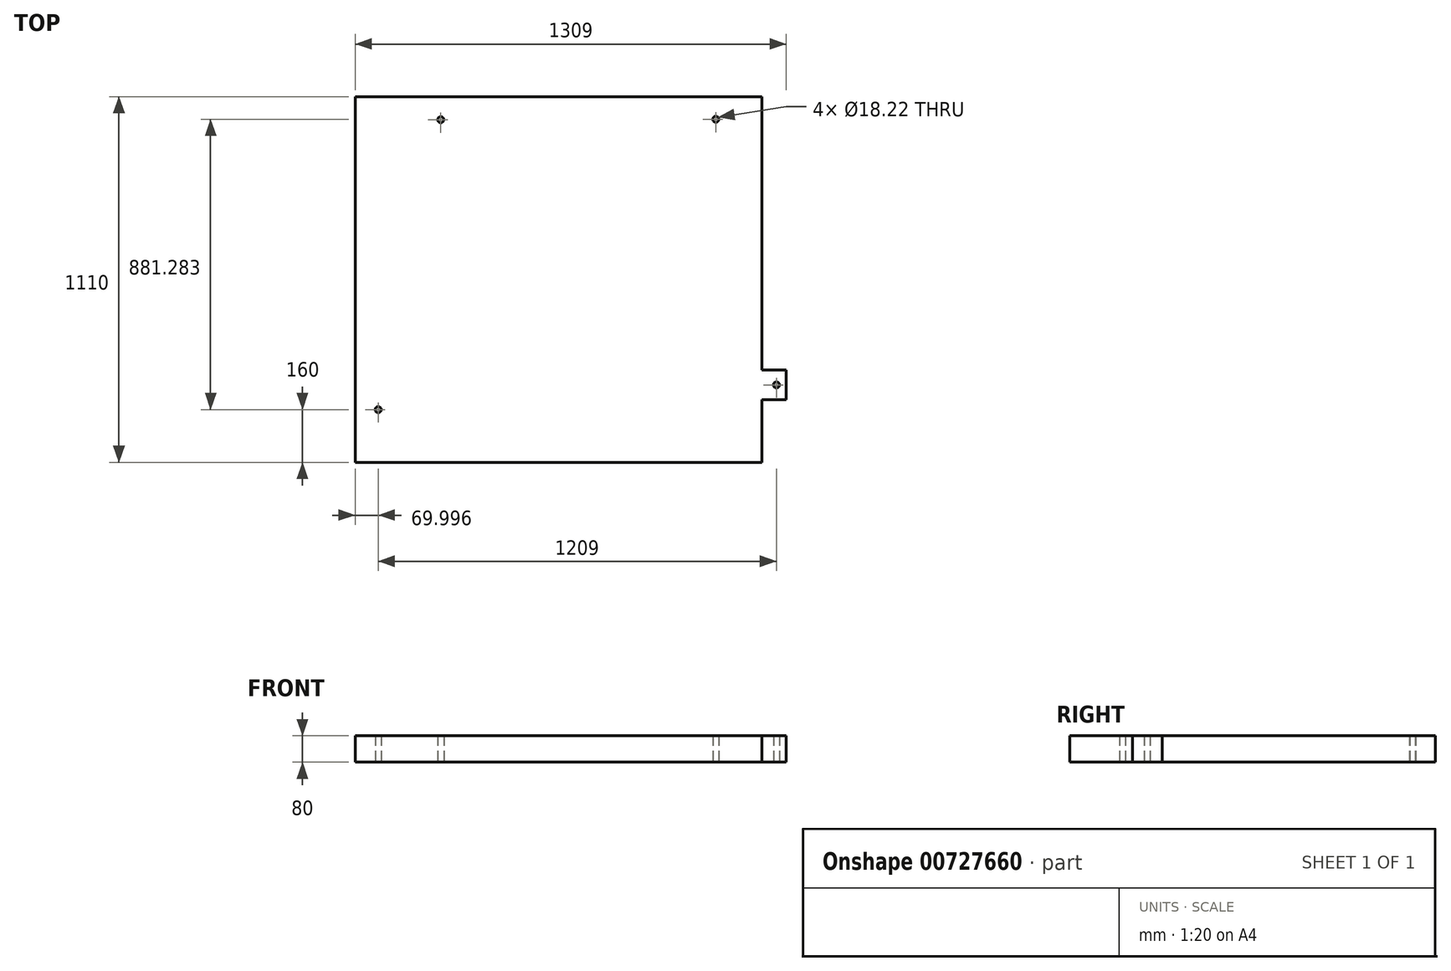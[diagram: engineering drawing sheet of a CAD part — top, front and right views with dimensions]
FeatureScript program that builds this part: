
annotation { "Feature Type Name" : "Feature", "Feature Type Description" : "" }
export const myFeature = defineFeature(function(context is Context, id is Id, definition is map)
    precondition{}
    {
        {
            var Q0;
            Q0=qCreatedBy(makeId("Top.planeOp"),FACE);
            var sketch = newSketch(context, id + "F0", { "sketchPlane" : qUnion([Q0])});
            skLineSegment(sketch, "E0.bottom", {"start": v(-626.11, 650.87) * mm, "end": v(608.89, 650.87) * mm});
            skLineSegment(sketch, "E0.top", {"start": v(-626.11, -459.13) * mm, "end": v(608.89, -459.13) * mm});
            skLineSegment(sketch, "E0.left", {"start": v(-626.11, 650.87) * mm, "end": v(-626.11, -459.13) * mm});
            skLineSegment(sketch, "E0.right", {"start": v(608.89, 650.87) * mm, "end": v(608.89, -459.13) * mm});
            skLineSegment(sketch, "E1.bottom", {"start": v(608.89, -179.13) * mm, "end": v(682.89, -179.13) * mm});
            skLineSegment(sketch, "E1.top", {"start": v(608.89, -269.13) * mm, "end": v(682.89, -269.13) * mm});
            skLineSegment(sketch, "E1.left", {"start": v(608.89, -179.13) * mm, "end": v(608.89, -269.13) * mm});
            skLineSegment(sketch, "E1.right", {"start": v(682.89, -179.13) * mm, "end": v(682.89, -269.13) * mm});
            skCircle(sketch, "E2", {"center": v(-556.11, -299.13) * mm, "radius": 9.1 * mm});
            skCircle(sketch, "E3", {"center": v(-366.11, 580.87) * mm, "radius": 9.1 * mm});
            skCircle(sketch, "E4", {"center": v(468.89, 582.15) * mm, "radius": 9.1 * mm});
            skCircle(sketch, "E5", {"center": v(652.89, -224.13) * mm, "radius": 9.1 * mm});
            skSolve(sketch);
        }
        {
            var Q0;
            {var subQ1=sQuery(id+"F0.wireOp",EDGE,"E0.bottom");Q0=makeQuery(id+"F0.imprint","IMPRINT",FACE,{"disambiguationData":[TD([[makeQuery(id+"F0.imprint","IMPRINT",EDGE,{"derivedFrom":subQ1}),-1.0]])]});}
            var Q1;
            Q1=makeQuery(id+"F0.imprint","IMPRINT",FACE,{"disambiguationData":[TD([[makeQuery(id+"F0.imprint","IMPRINT",EDGE,{"derivedFrom":sQuery(id+"F0.wireOp",EDGE,"E1.bottom")}),-1.0]])]});
            extrude(context, id + "F1", {"entities" : qUnion([Q0, Q1]), "depth" : 80 * mm, "offsetDistance" : 25 * mm});
        }
    });
